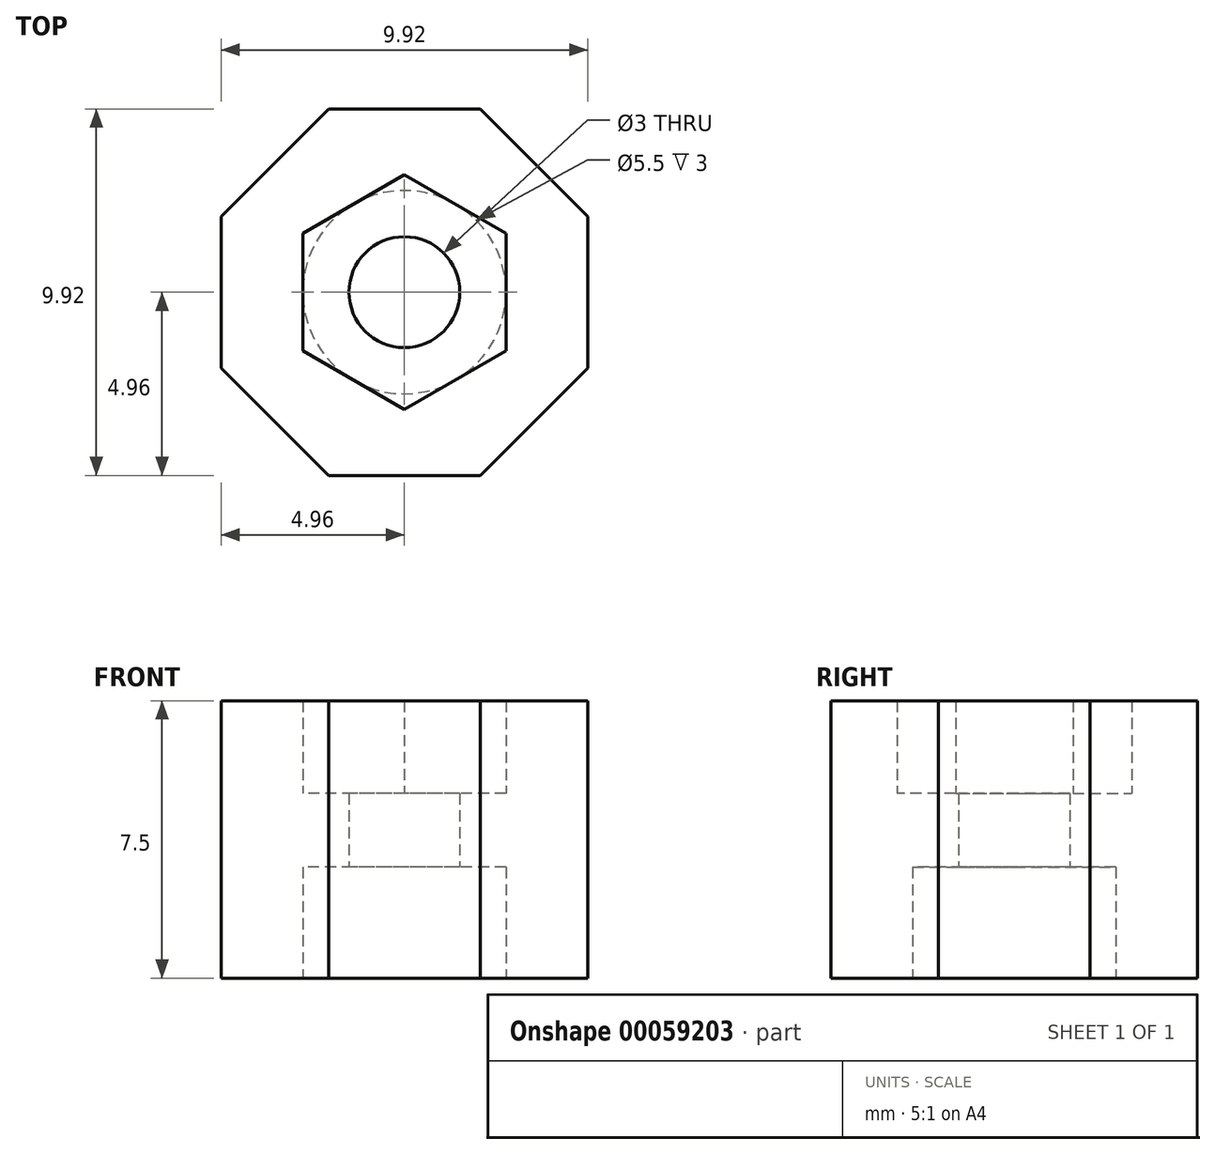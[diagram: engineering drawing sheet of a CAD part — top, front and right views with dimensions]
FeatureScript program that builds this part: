
annotation { "Feature Type Name" : "Feature", "Feature Type Description" : "" }
export const myFeature = defineFeature(function(context is Context, id is Id, definition is map)
    precondition{}
    {
        {
            var Q0;
            Q0=qCreatedBy(makeId("Top.planeOp"),FACE);
            var sketch = newSketch(context, id + "F0", { "sketchPlane" : qUnion([Q0])});
            skCircle(sketch, "E0", {"center": v(0, 0) * mm, "radius": 1.5 * mm});
            skCircle(sketch, "E1", {"center": v(0, 0) * mm, "radius": 2.75 * mm});
            skCircle(sketch, "E2.cCircle", {"center": v(0, 0) * mm, "radius": 2.75 * mm, "construction": true});
            skLineSegment(sketch, "E2.0", {"start": v(2.75, 1.59) * mm, "end": v(2.75, -1.59) * mm});
            skLineSegment(sketch, "E2.1", {"start": v(2.75, -1.59) * mm, "end": v(0, -3.18) * mm});
            skLineSegment(sketch, "E2.2", {"start": v(0, -3.18) * mm, "end": v(-2.75, -1.59) * mm});
            skLineSegment(sketch, "E2.3", {"start": v(-2.75, -1.59) * mm, "end": v(-2.75, 1.59) * mm});
            skLineSegment(sketch, "E2.4", {"start": v(-2.75, 1.59) * mm, "end": v(0, 3.18) * mm});
            skLineSegment(sketch, "E2.5", {"start": v(0, 3.18) * mm, "end": v(2.75, 1.59) * mm});
            skPoint(sketch, "E2.0.midPoint", {"position": v(2.75, 0) * mm});
            skCircle(sketch, "E3.cCircle", {"center": v(0, 0) * mm, "radius": 4.96 * mm, "construction": true});
            skLineSegment(sketch, "E3.0", {"start": v(-2.05, 4.96) * mm, "end": v(2.05, 4.96) * mm});
            skLineSegment(sketch, "E3.1", {"start": v(2.05, 4.96) * mm, "end": v(4.96, 2.05) * mm});
            skLineSegment(sketch, "E3.2", {"start": v(4.96, 2.05) * mm, "end": v(4.96, -2.05) * mm});
            skLineSegment(sketch, "E3.3", {"start": v(4.96, -2.05) * mm, "end": v(2.05, -4.96) * mm});
            skLineSegment(sketch, "E3.4", {"start": v(2.05, -4.96) * mm, "end": v(-2.05, -4.96) * mm});
            skLineSegment(sketch, "E3.5", {"start": v(-2.05, -4.96) * mm, "end": v(-4.96, -2.05) * mm});
            skLineSegment(sketch, "E3.6", {"start": v(-4.96, -2.05) * mm, "end": v(-4.96, 2.05) * mm});
            skLineSegment(sketch, "E3.7", {"start": v(-4.96, 2.05) * mm, "end": v(-2.05, 4.96) * mm});
            skPoint(sketch, "E3.0.midPoint", {"position": v(0, 4.96) * mm});
            skSolve(sketch);
        }
        {
            var Q0;
            Q0 = qSketchRegion(id + "F0", true);
            extrude(context, id + "F1", {"entities" : qUnion([Q0]), "depth" : 7.5 * mm});
        }
        {
            var Q0;
            {var subQ0=sQuery(id+"F0.wireOp",EDGE,"E2.4");var subQ1=sQuery(id+"F0.wireOp",EDGE,"E1");var subQ2=makeQuery(id+"F0.imprint","INTERSECT",VERTEX,{"derivedFrom":[subQ1,subQ0]});Q0=makeQuery(id+"F0.imprint","IMPRINT",FACE,{"disambiguationData":[TD([[makeQuery(id+"F0.imprint","IMPRINT",EDGE,{"disambiguationData":[TD([[subQ2,-1.0]])],"derivedFrom":subQ1}),-1.0]])]});}
            var Q1;
            {var subQ0=sQuery(id+"F0.wireOp",EDGE,"E2.5");var subQ1=sQuery(id+"F0.wireOp",EDGE,"E1");var subQ2=makeQuery(id+"F0.imprint","INTERSECT",VERTEX,{"derivedFrom":[subQ1,subQ0]});Q1=makeQuery(id+"F0.imprint","IMPRINT",FACE,{"disambiguationData":[TD([[makeQuery(id+"F0.imprint","IMPRINT",EDGE,{"disambiguationData":[TD([[subQ2,-1.0]])],"derivedFrom":subQ1}),-1.0]])]});}
            var Q2;
            {var subQ0=sQuery(id+"F0.wireOp",EDGE,"E2.5");var subQ1=sQuery(id+"F0.wireOp",EDGE,"E1");var subQ2=makeQuery(id+"F0.imprint","INTERSECT",VERTEX,{"derivedFrom":[subQ1,subQ0]});Q2=makeQuery(id+"F0.imprint","IMPRINT",FACE,{"disambiguationData":[TD([[makeQuery(id+"F0.imprint","IMPRINT",EDGE,{"disambiguationData":[TD([[subQ2,1.0]])],"derivedFrom":subQ1}),-1.0]])]});}
            var Q3;
            {var subQ0=sQuery(id+"F0.wireOp",EDGE,"E2.0");var subQ1=sQuery(id+"F0.wireOp",EDGE,"E1");var subQ2=makeQuery(id+"F0.imprint","INTERSECT",VERTEX,{"derivedFrom":[subQ1,subQ0]});Q3=makeQuery(id+"F0.imprint","IMPRINT",FACE,{"disambiguationData":[TD([[makeQuery(id+"F0.imprint","IMPRINT",EDGE,{"disambiguationData":[TD([[subQ2,1.0]])],"derivedFrom":subQ1}),-1.0]])]});}
            var Q4;
            {var subQ0=sQuery(id+"F0.wireOp",EDGE,"E2.2");var subQ1=sQuery(id+"F0.wireOp",EDGE,"E1");var subQ2=makeQuery(id+"F0.imprint","INTERSECT",VERTEX,{"derivedFrom":[subQ1,subQ0]});Q4=makeQuery(id+"F0.imprint","IMPRINT",FACE,{"disambiguationData":[TD([[makeQuery(id+"F0.imprint","IMPRINT",EDGE,{"disambiguationData":[TD([[subQ2,-1.0]])],"derivedFrom":subQ1}),-1.0]])]});}
            var Q5;
            {var subQ0=sQuery(id+"F0.wireOp",EDGE,"E2.3");var subQ1=sQuery(id+"F0.wireOp",EDGE,"E1");var subQ2=makeQuery(id+"F0.imprint","INTERSECT",VERTEX,{"derivedFrom":[subQ1,subQ0]});Q5=makeQuery(id+"F0.imprint","IMPRINT",FACE,{"disambiguationData":[TD([[makeQuery(id+"F0.imprint","IMPRINT",EDGE,{"disambiguationData":[TD([[subQ2,-1.0]])],"derivedFrom":subQ1}),-1.0]])]});}
            extrude(context, id + "F2", {"entities" : qUnion([Q0, Q1, Q2, Q3, Q4, Q5]), "operationType" : NewBodyOperationType.ADD, "depth" : (7.5 - 2.5) * mm});
        }
        {
            var Q0;
            Q0=makeQuery(id+"F0.imprint","IMPRINT",FACE,{"disambiguationData":[TD([[makeQuery(id+"F0.imprint","IMPRINT",EDGE,{"derivedFrom":sQuery(id+"F0.wireOp",EDGE,"E0")}),-1.0]])]});
            extrude(context, id + "F3", {"entities" : qUnion([Q0]), "operationType" : NewBodyOperationType.ADD, "depth" : (7.5 - 2.5) * mm});
        }
        {
            var Q0;
            Q0=makeQuery(id+"F0.imprint","IMPRINT",FACE,{"disambiguationData":[TD([[makeQuery(id+"F0.imprint","IMPRINT",EDGE,{"derivedFrom":sQuery(id+"F0.wireOp",EDGE,"E0")}),-1.0]])]});
            extrude(context, id + "F4", {"entities" : qUnion([Q0]), "operationType" : NewBodyOperationType.REMOVE, "depth" : 3 * mm});
        }
    });
